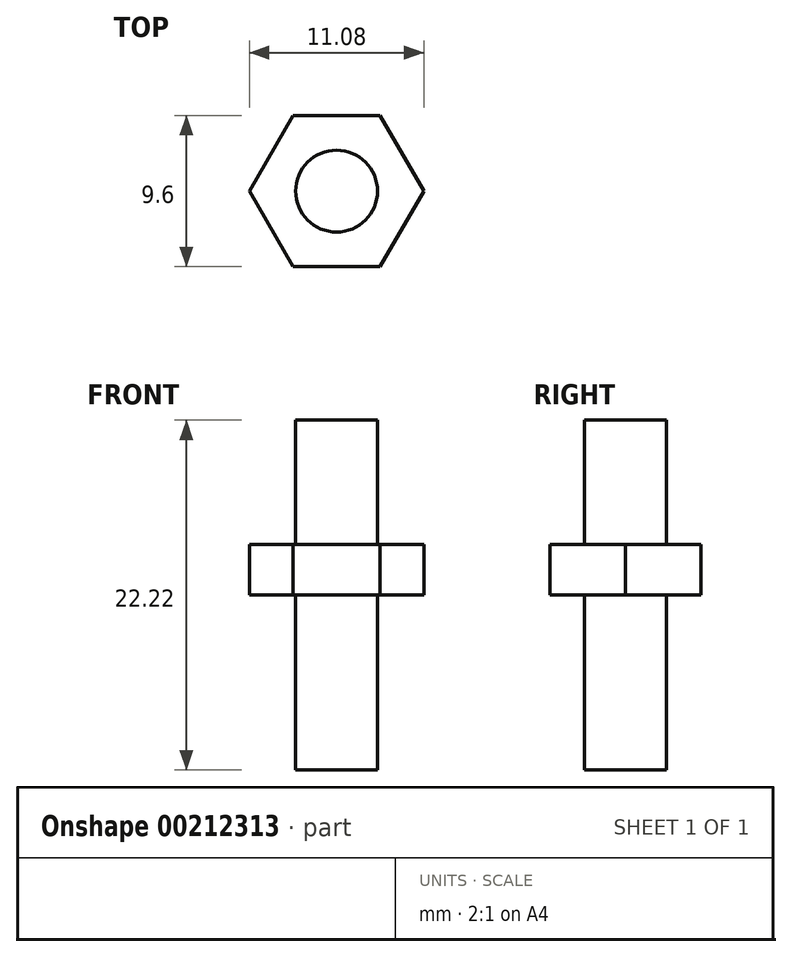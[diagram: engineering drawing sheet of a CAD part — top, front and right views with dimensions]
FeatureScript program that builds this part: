
annotation { "Feature Type Name" : "Feature", "Feature Type Description" : "" }
export const myFeature = defineFeature(function(context is Context, id is Id, definition is map)
    precondition{}
    {
        {
            var Q0;
            Q0=qCreatedBy(makeId("Top.planeOp"),FACE);
            var sketch = newSketch(context, id + "F0", { "sketchPlane" : qUnion([Q0])});
            skCircle(sketch, "E0.cCircle", {"center": v(0, 0) * mm, "radius": 4.8 * mm, "construction": true});
            skLineSegment(sketch, "E0.0", {"start": v(-2.77, 4.8) * mm, "end": v(2.77, 4.8) * mm});
            skLineSegment(sketch, "E0.1", {"start": v(2.77, 4.8) * mm, "end": v(5.54, 0) * mm});
            skLineSegment(sketch, "E0.2", {"start": v(5.54, 0) * mm, "end": v(2.77, -4.8) * mm});
            skLineSegment(sketch, "E0.3", {"start": v(2.77, -4.8) * mm, "end": v(-2.77, -4.8) * mm});
            skLineSegment(sketch, "E0.4", {"start": v(-2.77, -4.8) * mm, "end": v(-5.54, 0) * mm});
            skLineSegment(sketch, "E0.5", {"start": v(-5.54, 0) * mm, "end": v(-2.77, 4.8) * mm});
            skPoint(sketch, "E0.0.midPoint", {"position": v(0, 4.8) * mm});
            skCircle(sketch, "E1", {"center": v(0, 0) * mm, "radius": 2.6 * mm});
            skSolve(sketch);
        }
        {
            var Q0;
            Q0 = qSketchRegion(id + "F0", true);
            var Q1;
            Q1=makeQuery(id+"F0.imprint","IMPRINT",FACE,{"disambiguationData":[TD([[makeQuery(id+"F0.imprint","IMPRINT",EDGE,{"derivedFrom":sQuery(id+"F0.wireOp",EDGE,"E1")}),1.0]])]});
            extrude(context, id + "F1", {"entities" : qUnion([Q0, Q1]), "depth" : 3.2 * mm});
        }
        {
            var Q0;
            Q0=makeQuery(id+"F0.imprint","IMPRINT",FACE,{"disambiguationData":[TD([[makeQuery(id+"F0.imprint","IMPRINT",EDGE,{"derivedFrom":sQuery(id+"F0.wireOp",EDGE,"E1")}),1.0]])]});
            var Q1;
            Q1=sQuery(id+"F0.wireOp",EDGE,"E1");
            extrude(context, id + "F2", {"entities" : qUnion([Q0]), "operationType" : NewBodyOperationType.ADD, "surfaceEntities" : qUnion([Q1]), "depth" : 11.1 * mm, "hasSecondDirection" : true, "secondDirectionOppositeDirection" : true, "secondDirectionDepth" : 11.1 * mm});
        }
    });
